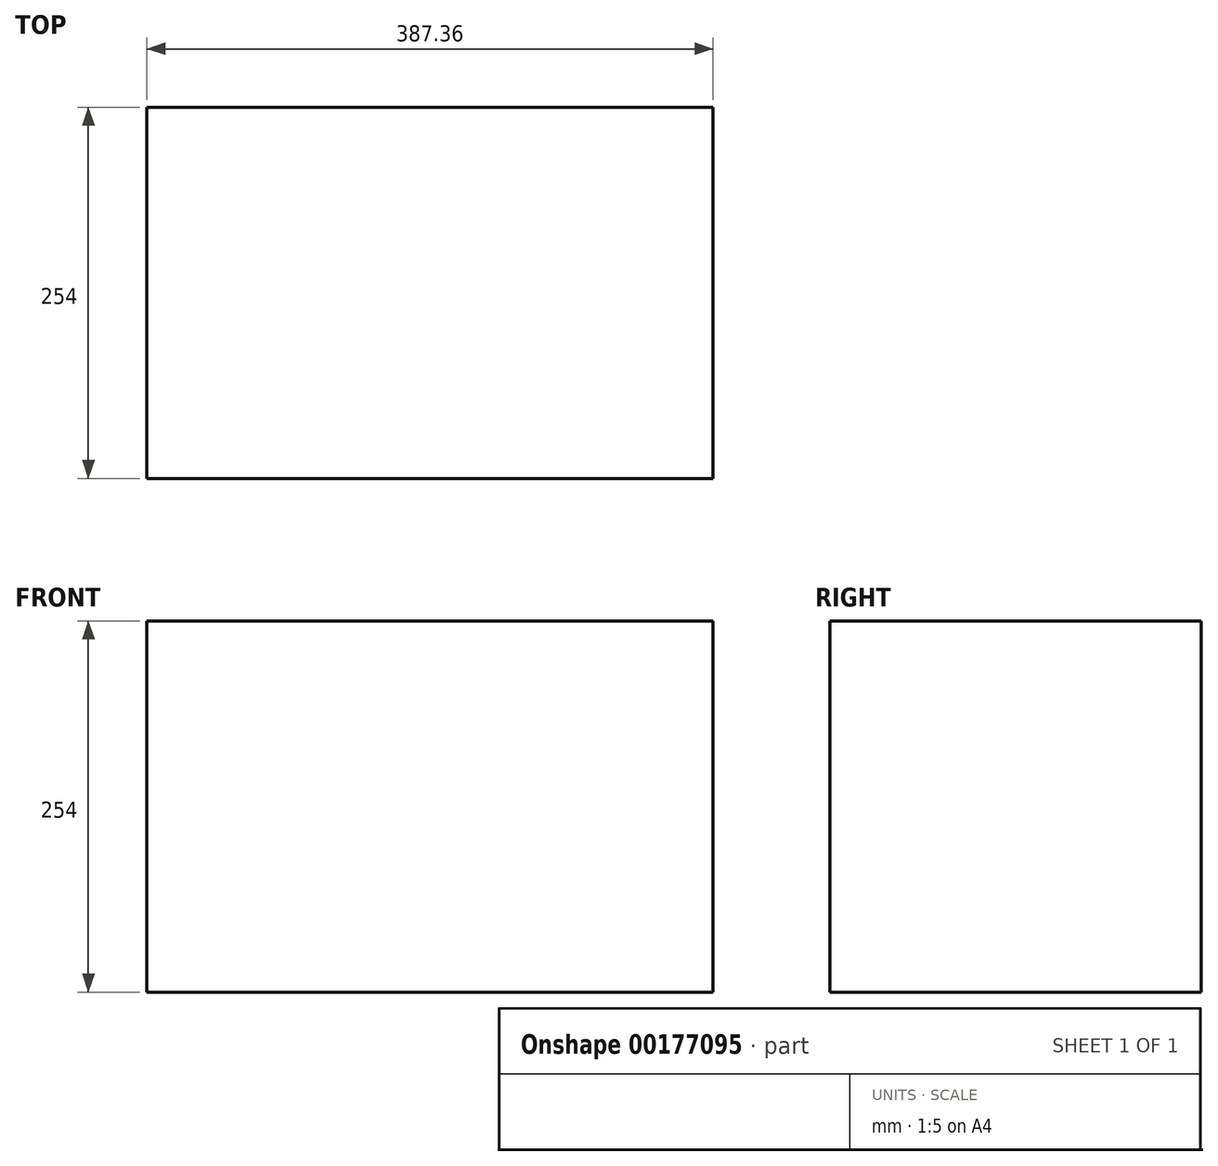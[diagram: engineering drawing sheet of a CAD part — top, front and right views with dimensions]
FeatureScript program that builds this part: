
annotation { "Feature Type Name" : "Feature", "Feature Type Description" : "" }
export const myFeature = defineFeature(function(context is Context, id is Id, definition is map)
    precondition{}
    {
        {
            var Q0;
            Q0=qCreatedBy(makeId("Front.planeOp"),FACE);
            var sketch = newSketch(context, id + "F0", { "sketchPlane" : qUnion([Q0])});
            skLineSegment(sketch, "E0.bottom", {"start": v(-193.67, 127) * mm, "end": v(193.68, 127) * mm});
            skLineSegment(sketch, "E0.top", {"start": v(-193.68, -127) * mm, "end": v(193.67, -127) * mm});
            skLineSegment(sketch, "E0.left", {"start": v(-193.67, 127) * mm, "end": v(-193.68, -127) * mm});
            skLineSegment(sketch, "E0.right", {"start": v(193.68, 127) * mm, "end": v(193.67, -127) * mm});
            skPoint(sketch, "E0.middle", {"position": v(0, 0) * mm});
            skSolve(sketch);
        }
        {
            var Q0;
            Q0=makeQuery(id+"F0.imprint","IMPRINT",FACE,{"disambiguationData":[TD([[makeQuery(id+"F0.imprint","IMPRINT",EDGE,{"derivedFrom":sQuery(id+"F0.wireOp",EDGE,"E0.bottom")}),-1.0]])]});
            extrude(context, id + "F1", {"entities" : qUnion([Q0]), "depth" : 254 * mm});
        }
    });
